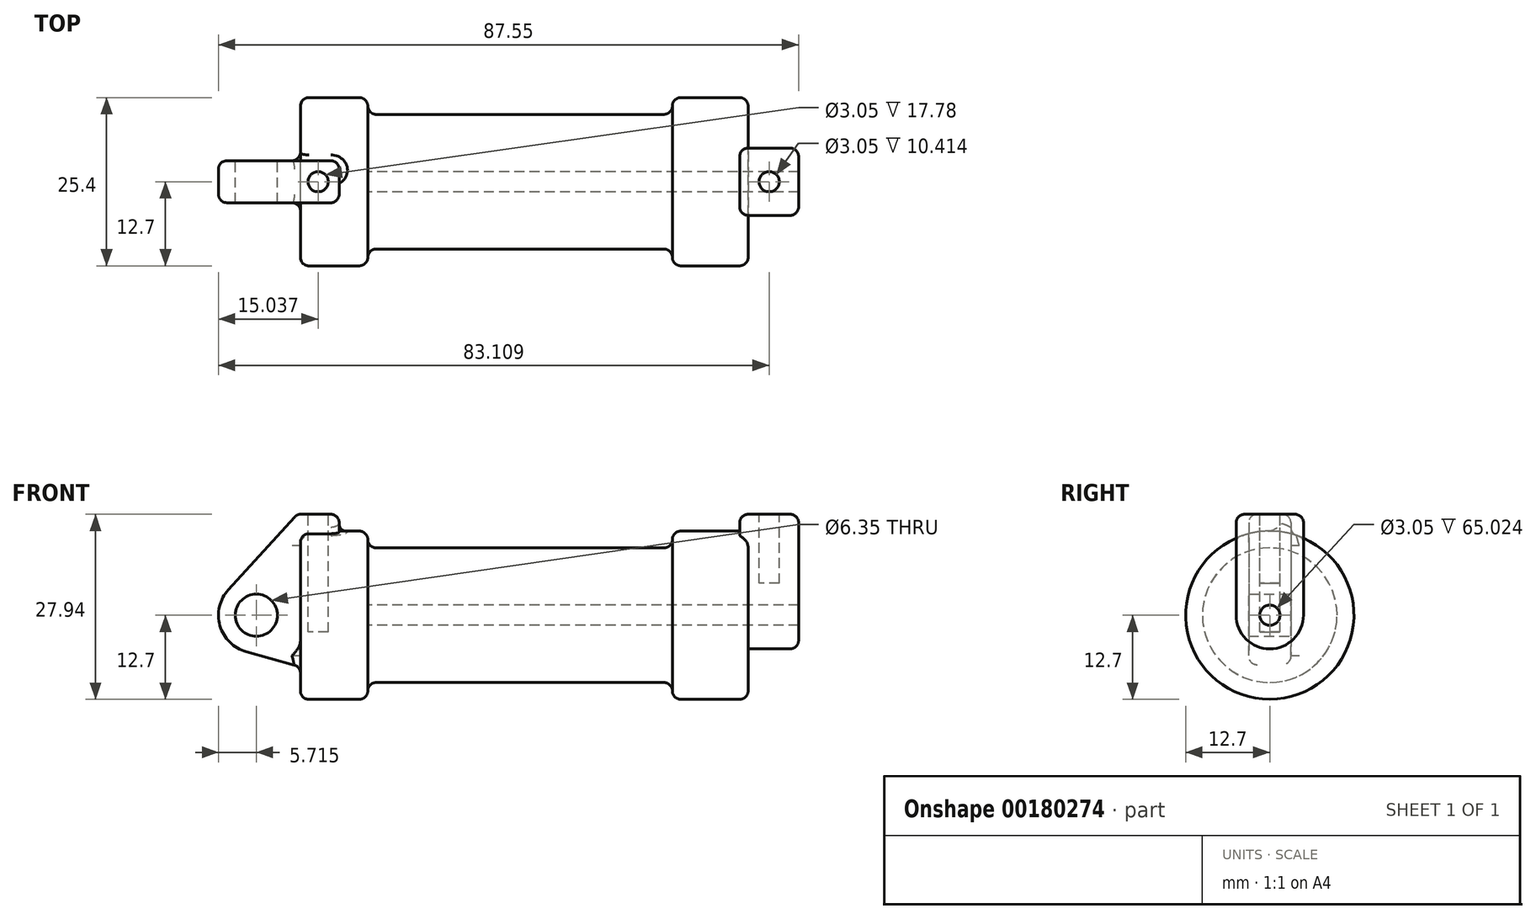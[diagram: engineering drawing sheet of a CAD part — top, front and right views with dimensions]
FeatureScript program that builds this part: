
annotation { "Feature Type Name" : "Feature", "Feature Type Description" : "" }
export const myFeature = defineFeature(function(context is Context, id is Id, definition is map)
    precondition{}
    {
        {
            var Q0;
            Q0=qCreatedBy(makeId("Front.planeOp"),FACE);
            var sketch = newSketch(context, id + "F0", { "sketchPlane" : qUnion([Q0])});
            skLineSegment(sketch, "E0", {"start": v(0, 0) * mm, "end": v(0, 12.7) * mm});
            skLineSegment(sketch, "E1", {"start": v(0, 12.7) * mm, "end": v(10.16, 12.7) * mm});
            skLineSegment(sketch, "E2", {"start": v(10.16, 12.7) * mm, "end": v(10.16, 10.16) * mm});
            skLineSegment(sketch, "E3", {"start": v(10.16, 10.16) * mm, "end": v(56.13, 10.16) * mm});
            skLineSegment(sketch, "E4", {"start": v(56.13, 10.16) * mm, "end": v(56.13, 12.7) * mm});
            skLineSegment(sketch, "E5", {"start": v(56.13, 12.7) * mm, "end": v(66.3, 12.7) * mm});
            skLineSegment(sketch, "E6", {"start": v(66.3, 12.7) * mm, "end": v(66.3, 0) * mm});
            skLineSegment(sketch, "E7", {"start": v(66.3, 0) * mm, "end": v(0, 0) * mm});
            skLineSegment(sketch, "E8", {"start": v(5.84, 15.24) * mm, "end": v(-0.5, 15.24) * mm});
            skLineSegment(sketch, "E9", {"start": v(-0.5, 15.24) * mm, "end": v(-10.88, 3.85) * mm});
            skLineSegment(sketch, "E10", {"start": v(0, 0) * mm, "end": v(-6.65, 0) * mm});
            skCircle(sketch, "E11", {"center": v(-6.65, 0) * mm, "radius": 5.72 * mm});
            skCircle(sketch, "E12", {"center": v(-6.65, 0) * mm, "radius": 3.18 * mm});
            skLineSegment(sketch, "E13", {"start": v(5.84, 15.24) * mm, "end": v(5.84, -9.4) * mm});
            skLineSegment(sketch, "E14", {"start": v(5.84, -9.4) * mm, "end": v(-8.18, -5.5) * mm});
            skSolve(sketch);
        }
        {
            var Q0;
            {var subQ0=sQuery(id+"F0.wireOp",EDGE,"E0");Q0=makeQuery(id+"F0.imprint","IMPRINT",FACE,{"disambiguationData":[TD([[makeQuery(id+"F0.imprint","IMPRINT",EDGE,{"derivedFrom":subQ0}),-1.0]])]});}
            var Q1;
            {var subQ0=sQuery(id+"F0.wireOp",EDGE,"E2");Q1=makeQuery(id+"F0.imprint","IMPRINT",FACE,{"disambiguationData":[TD([[makeQuery(id+"F0.imprint","IMPRINT",EDGE,{"derivedFrom":subQ0}),-1.0]])]});}
            var Q2;
            Q2=sQuery(id+"F0.wireOp",EDGE,"E7");
            revolve(context, id + "F1", {"entities" : qUnion([Q0, Q1]), "axis" : qUnion([Q2]), "revolveType" : RevolveType.FULL});
        }
        {
            var Q0;
            {var subQ3=sQuery(id+"F0.wireOp",EDGE,"E0");Q0=makeQuery(id+"F0.imprint","IMPRINT",FACE,{"disambiguationData":[TD([[makeQuery(id+"F0.imprint","IMPRINT",EDGE,{"derivedFrom":subQ3}),1.0]])]});}
            var Q1;
            {var subQ0=sQuery(id+"F0.wireOp",EDGE,"E14");Q1=makeQuery(id+"F0.imprint","IMPRINT",FACE,{"disambiguationData":[TD([[makeQuery(id+"F0.imprint","IMPRINT",EDGE,{"derivedFrom":subQ0}),-1.0]])]});}
            var Q2;
            {var subQ4=sQuery(id+"F0.wireOp",EDGE,"E12");Q2=makeQuery(id+"F0.imprint","IMPRINT",FACE,{"disambiguationData":[TD([[makeQuery(id+"F0.imprint","IMPRINT",EDGE,{"derivedFrom":subQ4}),-1.0]])]});}
            var Q3;
            {var subQ0=sQuery(id+"F0.wireOp",EDGE,"E0");Q3=makeQuery(id+"F0.imprint","IMPRINT",FACE,{"disambiguationData":[TD([[makeQuery(id+"F0.imprint","IMPRINT",EDGE,{"derivedFrom":subQ0}),-1.0]])]});}
            extrude(context, id + "F2", {"entities" : qUnion([Q0, Q1, Q2, Q3]), "operationType" : NewBodyOperationType.ADD, "endBound" : BoundingType.SYMMETRIC, "depth" : 6.35 * mm});
        }
        {
            var Q0;
            Q0=makeQuery(id+"F1.opRevolve","SWEPT_FACE",FACE,{"disambiguationData":[OSD([sQuery(id+"F0.wireOp",EDGE,"E6")])]});
            var sketch = newSketch(context, id + "F3", { "sketchPlane" : qUnion([Q0])});
            skCircle(sketch, "E15", {"center": v(0, 0) * mm, "radius": 1.52 * mm});
            skCircle(sketch, "E16", {"center": v(0, 0) * mm, "radius": 5.08 * mm});
            skLineSegment(sketch, "E17", {"start": v(-5.08, 0) * mm, "end": v(-5.08, 15.24) * mm});
            skLineSegment(sketch, "E18", {"start": v(5.08, 0) * mm, "end": v(5.08, 15.24) * mm});
            skLineSegment(sketch, "E19", {"start": v(-5.08, 15.24) * mm, "end": v(5.08, 15.24) * mm});
            skSolve(sketch);
        }
        {
            var Q0;
            Q0=makeQuery(id+"F3.imprint","IMPRINT",FACE,{"disambiguationData":[TD([[makeQuery(id+"F3.imprint","IMPRINT",EDGE,{"derivedFrom":sQuery(id+"F3.wireOp",EDGE,"E15")}),-1.0]])]});
            var Q1;
            {var subQ0=sQuery(id+"F3.wireOp",EDGE,"E17");var subQ1=sQuery(id+"F3.wireOp",EDGE,"E16");var subQ2=makeQuery(id+"F3.imprint","INTERSECT",VERTEX,{"derivedFrom":[subQ1,subQ0]});Q1=makeQuery(id+"F3.imprint","IMPRINT",FACE,{"disambiguationData":[TD([[makeQuery(id+"F3.imprint","IMPRINT",EDGE,{"disambiguationData":[TD([[subQ2,1.0]])],"derivedFrom":subQ1}),-1.0]])]});}
            var Q2;
            {var subQ0=sQuery(id+"F3.wireOp",EDGE,"E19");Q2=makeQuery(id+"F3.imprint","IMPRINT",FACE,{"disambiguationData":[TD([[makeQuery(id+"F3.imprint","IMPRINT",EDGE,{"derivedFrom":subQ0}),-1.0]])]});}
            extrude(context, id + "F4", {"entities" : qUnion([Q0, Q1, Q2]), "operationType" : NewBodyOperationType.ADD, "depth" : 7.62 * mm});
        }
        {
            var Q0;
            Q0=makeQuery(id+"F4.boolean.opBoolean","SPLIT",FACE,{"disambiguationData":[TD([makeQuery(id+"F1.opRevolve","SWEPT_FACE",FACE,{"disambiguationData":[OSD([sQuery(id+"F0.wireOp",EDGE,"E5")])]})])],"derivedFrom":makeQuery(id+"F1.opRevolve","SWEPT_FACE",FACE,{"disambiguationData":[OSD([sQuery(id+"F0.wireOp",EDGE,"E6")])]})});
            var Q1;
            Q1=makeQuery(id+"F4.opExtrude","CAP_FACE",FACE,{"disambiguationData":[OSD([sQuery(id+"F3.wireOp",EDGE,"E15"),sQuery(id+"F3.wireOp",EDGE,"E16"),sQuery(id+"F3.wireOp",EDGE,"E17"),sQuery(id+"F3.wireOp",EDGE,"E18"),sQuery(id+"F3.wireOp",EDGE,"E19")])],"isStart":false});
            extrude(context, id + "F5", {"entities" : qUnion([Q0, Q1]), "operationType" : NewBodyOperationType.ADD, "depth" : 1.27 * mm});
        }
        {
            var Q0;
            Q0=makeQuery(id+"F3.imprint","IMPRINT",FACE,{"disambiguationData":[TD([[makeQuery(id+"F3.imprint","IMPRINT",EDGE,{"derivedFrom":sQuery(id+"F3.wireOp",EDGE,"E15")}),1.0]])]});
            var Q1;
            Q1=makeQuery(id+"F1.opRevolve","SWEPT_FACE",FACE,{"disambiguationData":[OSD([sQuery(id+"F0.wireOp",EDGE,"E2")])]});
            extrude(context, id + "F6", {"entities" : qUnion([Q0]), "operationType" : NewBodyOperationType.REMOVE, "endBound" : BoundingType.UP_TO_SURFACE, "oppositeDirection" : true, "endBoundEntityFace" : qUnion([Q1]), "depth" : 25.4 * mm});
        }
        {
            var Q0;
            Q0=makeQuery(id+"F2.opExtrude","SWEPT_FACE",FACE,{"disambiguationData":[OSD([sQuery(id+"F0.wireOp",EDGE,"E8")])]});
            var sketch = newSketch(context, id + "F7", { "sketchPlane" : qUnion([Q0])});
            skCircle(sketch, "E20", {"center": v(2.67, 0) * mm, "radius": 1.52 * mm});
            skPoint(sketch, "E20.centerSnap0", {"position": v(5.84, 0) * mm});
            skPoint(sketch, "E20.centerSnap1", {"position": v(2.67, -3.18) * mm});
            skLineSegment(sketch, "E21.0", {"start": v(75.18, 5.08) * mm, "end": v(66.3, 5.08) * mm});
            skLineSegment(sketch, "E22.0", {"start": v(66.3, -5.08) * mm, "end": v(66.3, 5.08) * mm});
            skLineSegment(sketch, "E23.0", {"start": v(75.18, -5.08) * mm, "end": v(66.3, -5.08) * mm});
            skLineSegment(sketch, "E24.0", {"start": v(75.18, -5.08) * mm, "end": v(75.18, 5.08) * mm});
            skLineSegment(sketch, "E25", {"start": v(70.74, 5.08) * mm, "end": v(70.74, -5.08) * mm, "construction": true});
            skLineSegment(sketch, "E26", {"start": v(75.18, 0) * mm, "end": v(66.3, 0) * mm, "construction": true});
            skCircle(sketch, "E27", {"center": v(70.74, 0) * mm, "radius": 1.52 * mm});
            skSolve(sketch);
        }
        {
            var Q0;
            Q0=makeQuery(id+"F7.imprint","IMPRINT",FACE,{"disambiguationData":[TD([[makeQuery(id+"F7.imprint","IMPRINT",EDGE,{"derivedFrom":sQuery(id+"F7.wireOp",EDGE,"E20")}),1.0]])]});
            extrude(context, id + "F8", {"entities" : qUnion([Q0]), "operationType" : NewBodyOperationType.REMOVE, "oppositeDirection" : true, "depth" : 17.78 * mm});
        }
        {
            var Q0;
            Q0=makeQuery(id+"F7.imprint","IMPRINT",FACE,{"disambiguationData":[TD([[makeQuery(id+"F7.imprint","IMPRINT",EDGE,{"derivedFrom":sQuery(id+"F7.wireOp",EDGE,"E27")}),1.0]])]});
            extrude(context, id + "F9", {"entities" : qUnion([Q0]), "operationType" : NewBodyOperationType.REMOVE, "oppositeDirection" : true, "depth" : 10.4 * mm});
        }
        {
            var Q0;
            Q0=makeQuery(id+"F1.opRevolve","SWEPT_EDGE",EDGE,{"disambiguationData":[OSD([sQuery(id+"F0.wireOp",EDGE,"E2"),sQuery(id+"F0.wireOp",EDGE,"E3")])]});
            var Q1;
            Q1=makeQuery(id+"F1.opRevolve","SWEPT_EDGE",EDGE,{"disambiguationData":[OSD([sQuery(id+"F0.wireOp",EDGE,"E1"),sQuery(id+"F0.wireOp",EDGE,"E2")])]});
            var Q2;
            Q2=makeQuery(id+"F1.opRevolve","SWEPT_EDGE",EDGE,{"disambiguationData":[OSD([sQuery(id+"F0.wireOp",EDGE,"E0"),sQuery(id+"F0.wireOp",EDGE,"E1")])]});
            var Q3;
            Q3=makeQuery(id+"F1.opRevolve","SWEPT_EDGE",EDGE,{"disambiguationData":[OSD([sQuery(id+"F0.wireOp",EDGE,"E4"),sQuery(id+"F0.wireOp",EDGE,"E5")])]});
            var Q4;
            Q4=makeQuery(id+"F5.opExtrude","CAP_EDGE",EDGE,{"disambiguationData":[OSD([sQuery(id+"F0.wireOp",EDGE,"E5"),sQuery(id+"F0.wireOp",EDGE,"E6")])],"isStart":false});
            var Q5;
            Q5=makeQuery(id+"F1.opRevolve","SWEPT_EDGE",EDGE,{"disambiguationData":[OSD([sQuery(id+"F0.wireOp",EDGE,"E3"),sQuery(id+"F0.wireOp",EDGE,"E4")])]});
            fillet(context, id + "F10", {"entities" : qUnion([Q0, Q1, Q2, Q3, Q4, Q5]), "radius" : 1.27 * mm, "tangentPropagation" : true, "allowEdgeOverflow" : false});
        }
        {
            var Q0;
            Q0=makeQuery(id+"F2.boolean.opBoolean","INTERSECT",EDGE,{"derivedFrom":[makeQuery(id+"F1.opRevolve","SWEPT_FACE",FACE,{"disambiguationData":[OSD([sQuery(id+"F0.wireOp",EDGE,"E1")])]}),makeQuery(id+"F2.opExtrude","CAP_FACE",FACE,{"disambiguationData":[OSD([sQuery(id+"F0.wireOp",EDGE,"E8"),sQuery(id+"F0.wireOp",EDGE,"E9"),sQuery(id+"F0.wireOp",EDGE,"E11"),sQuery(id+"F0.wireOp",EDGE,"E12"),sQuery(id+"F0.wireOp",EDGE,"E13"),sQuery(id+"F0.wireOp",EDGE,"E14")])],"isStart":true})]});
            var Q1;
            Q1=makeQuery(id+"F2.opExtrude","CAP_EDGE",EDGE,{"disambiguationData":[OSD([sQuery(id+"F0.wireOp",EDGE,"E13")])],"isStart":true});
            var Q2;
            Q2=makeQuery(id+"F2.opExtrude","CAP_EDGE",EDGE,{"disambiguationData":[OSD([sQuery(id+"F0.wireOp",EDGE,"E8")])],"isStart":true});
            var Q3;
            Q3=makeQuery(id+"F2.opExtrude","CAP_EDGE",EDGE,{"disambiguationData":[OSD([sQuery(id+"F0.wireOp",EDGE,"E9")])],"isStart":true});
            var Q4;
            Q4=makeQuery(id+"F2.opExtrude","CAP_EDGE",EDGE,{"disambiguationData":[OSD([sQuery(id+"F0.wireOp",EDGE,"E11")])],"isStart":true});
            var Q5;
            Q5=makeQuery(id+"F2.opExtrude","CAP_EDGE",EDGE,{"disambiguationData":[OSD([sQuery(id+"F0.wireOp",EDGE,"E14")])],"isStart":true});
            var Q6;
            Q6=makeQuery(id+"F2.boolean.opBoolean","INTERSECT",EDGE,{"derivedFrom":[makeQuery(id+"F1.opRevolve","SWEPT_FACE",FACE,{"disambiguationData":[OSD([sQuery(id+"F0.wireOp",EDGE,"E0")])]}),makeQuery(id+"F2.opExtrude","CAP_FACE",FACE,{"disambiguationData":[OSD([sQuery(id+"F0.wireOp",EDGE,"E8"),sQuery(id+"F0.wireOp",EDGE,"E9"),sQuery(id+"F0.wireOp",EDGE,"E11"),sQuery(id+"F0.wireOp",EDGE,"E12"),sQuery(id+"F0.wireOp",EDGE,"E13"),sQuery(id+"F0.wireOp",EDGE,"E14")])],"isStart":true})]});
            var Q7;
            Q7=makeQuery(id+"F10.opFillet","BLEND_EDGE",EDGE,{"blendedFrom":[makeQuery(id+"F1.opRevolve","SWEPT_EDGE",EDGE,{"disambiguationData":[OSD([sQuery(id+"F0.wireOp",EDGE,"E0"),sQuery(id+"F0.wireOp",EDGE,"E1")])]}),makeQuery(id+"F2.opExtrude","CAP_FACE",FACE,{"disambiguationData":[OSD([sQuery(id+"F0.wireOp",EDGE,"E8"),sQuery(id+"F0.wireOp",EDGE,"E9"),sQuery(id+"F0.wireOp",EDGE,"E11"),sQuery(id+"F0.wireOp",EDGE,"E12"),sQuery(id+"F0.wireOp",EDGE,"E13"),sQuery(id+"F0.wireOp",EDGE,"E14")])],"isStart":true})],"blendedInto":[makeQuery(id+"F2.opExtrude","CAP_FACE",FACE,{"disambiguationData":[OSD([sQuery(id+"F0.wireOp",EDGE,"E8"),sQuery(id+"F0.wireOp",EDGE,"E9"),sQuery(id+"F0.wireOp",EDGE,"E11"),sQuery(id+"F0.wireOp",EDGE,"E12"),sQuery(id+"F0.wireOp",EDGE,"E13"),sQuery(id+"F0.wireOp",EDGE,"E14")])],"isStart":true})]});
            var Q8;
            Q8=makeQuery(id+"F2.opExtrude","SWEPT_FACE",FACE,{"disambiguationData":[OSD([sQuery(id+"F0.wireOp",EDGE,"E14")])]});
            var Q9;
            Q9=makeQuery(id+"F2.opExtrude","SWEPT_EDGE",EDGE,{"disambiguationData":[OSD([sQuery(id+"F0.wireOp",EDGE,"E8"),sQuery(id+"F0.wireOp",EDGE,"E13")])]});
            var Q10;
            Q10=makeQuery(id+"F2.opExtrude","CAP_EDGE",EDGE,{"disambiguationData":[OSD([sQuery(id+"F0.wireOp",EDGE,"E8")])],"isStart":false});
            var Q11;
            Q11=makeQuery(id+"F2.opExtrude","CAP_EDGE",EDGE,{"disambiguationData":[OSD([sQuery(id+"F0.wireOp",EDGE,"E13")])],"isStart":false});
            var Q12;
            Q12=makeQuery(id+"F2.opExtrude","SWEPT_FACE",FACE,{"disambiguationData":[OSD([sQuery(id+"F0.wireOp",EDGE,"E9")])]});
            fillet(context, id + "F11", {"entities" : qUnion([Q0, Q1, Q2, Q3, Q4, Q5, Q6, Q7, Q8, Q9, Q10, Q11, Q12]), "radius" : 1.27 * mm, "tangentPropagation" : true, "allowEdgeOverflow" : false});
        }
        {
            var Q0;
            {var subQ0=sQuery(id+"F3.wireOp",EDGE,"E19");var subQ1=sQuery(id+"F3.wireOp",EDGE,"E18");Q0=makeQuery(id+"F5.boolean.opBoolean","MERGE",EDGE,{"derivedFrom":[makeQuery(id+"F4.opExtrude","SWEPT_EDGE",EDGE,{"disambiguationData":[OSD([subQ1,subQ0])]}),makeQuery(id+"F5.opExtrude","SWEPT_EDGE",EDGE,{"disambiguationData":[OSD([subQ1,subQ0])]})]});}
            var Q1;
            {var subQ0=sQuery(id+"F3.wireOp",EDGE,"E16");var subQ1=sQuery(id+"F3.wireOp",EDGE,"E18");Q1=makeQuery(id+"F5.opExtrude","CAP_EDGE",EDGE,{"disambiguationData":[OSD([subQ1]),TDD([makeQuery(id+"F4.boolean.opBoolean","SPLIT",EDGE,{"disambiguationData":[TD([makeQuery(id+"F4.opExtrude","SWEPT_FACE",FACE,{"disambiguationData":[OSD([subQ0])]})])],"derivedFrom":makeQuery(id+"F4.opExtrude","CAP_EDGE",EDGE,{"disambiguationData":[OSD([subQ1])],"isStart":true})})])],"isStart":false});}
            var Q2;
            {var subQ0=sQuery(id+"F3.wireOp",EDGE,"E18");Q2=makeQuery(id+"F5.opExtrude","CAP_EDGE",EDGE,{"disambiguationData":[OSD([subQ0]),TDD([makeQuery(id+"F4.opExtrude","CAP_EDGE",EDGE,{"disambiguationData":[OSD([subQ0])],"isStart":false})])],"isStart":false});}
            var Q3;
            Q3=makeQuery(id+"F5.opExtrude","CAP_EDGE",EDGE,{"disambiguationData":[OSD([sQuery(id+"F3.wireOp",EDGE,"E19")])],"isStart":false});
            var Q4;
            {var subQ0=sQuery(id+"F3.wireOp",EDGE,"E19");var subQ1=sQuery(id+"F3.wireOp",EDGE,"E17");Q4=makeQuery(id+"F5.boolean.opBoolean","MERGE",EDGE,{"derivedFrom":[makeQuery(id+"F4.opExtrude","SWEPT_EDGE",EDGE,{"disambiguationData":[OSD([subQ1,subQ0])]}),makeQuery(id+"F5.opExtrude","SWEPT_EDGE",EDGE,{"disambiguationData":[OSD([subQ1,subQ0])]})]});}
            var Q5;
            Q5=makeQuery(id+"F4.opExtrude","CAP_EDGE",EDGE,{"disambiguationData":[OSD([sQuery(id+"F3.wireOp",EDGE,"E19")])],"isStart":true});
            var Q6;
            Q6=makeQuery(id+"F4.boolean.opBoolean","SPLIT",EDGE,{"disambiguationData":[OD(0.0)],"derivedFrom":makeQuery(id+"F1.opRevolve","SWEPT_EDGE",EDGE,{"disambiguationData":[OSD([sQuery(id+"F0.wireOp",EDGE,"E5"),sQuery(id+"F0.wireOp",EDGE,"E6")])]})});
            var Q7;
            {var subQ0=sQuery(id+"F3.wireOp",EDGE,"E17");var subQ1=sQuery(id+"F3.wireOp",EDGE,"E19");Q7=makeQuery(id+"F4.boolean.opBoolean","SPLIT",EDGE,{"disambiguationData":[TD([makeQuery(id+"F4.opExtrude","SWEPT_FACE",FACE,{"disambiguationData":[OSD([subQ1])]})])],"derivedFrom":makeQuery(id+"F4.opExtrude","CAP_EDGE",EDGE,{"disambiguationData":[OSD([subQ0])],"isStart":true})});}
            var Q8;
            {var subQ0=sQuery(id+"F3.wireOp",EDGE,"E18");var subQ1=sQuery(id+"F3.wireOp",EDGE,"E19");Q8=makeQuery(id+"F4.boolean.opBoolean","SPLIT",EDGE,{"disambiguationData":[TD([makeQuery(id+"F4.opExtrude","SWEPT_FACE",FACE,{"disambiguationData":[OSD([subQ1])]})])],"derivedFrom":makeQuery(id+"F4.opExtrude","CAP_EDGE",EDGE,{"disambiguationData":[OSD([subQ0])],"isStart":true})});}
            fillet(context, id + "F12", {"entities" : qUnion([Q0, Q1, Q2, Q3, Q4, Q5, Q6, Q7, Q8]), "radius" : 1.27 * mm, "tangentPropagation" : true, "allowEdgeOverflow" : false});
        }
    });
